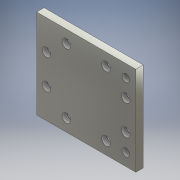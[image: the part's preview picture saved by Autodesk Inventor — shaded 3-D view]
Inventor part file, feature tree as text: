
AUTODESK INVENTOR PART (.ipt)
format: ipt  version: 2017 (Build 210142000, 142)  size: 217,088 bytes
history: native  units: mm
features: extrude x3, sketch x3, projected_geometry x1
ambient origin geometry x8: Origin, YZ Plane, XZ Plane, XY Plane, X Axis, Y Axis, Z Axis, Center Point
bodies: Solid1 (feature_tree)
feature tree (7):
  extrude  "Extrusion1"  Depth=3.0mm TaperAngle=0.0deg
  extrude  "Extrusion2"  Depth=3.0mm TaperAngle=0.0deg
  extrude  "Extrusion4"  Depth=3.0mm
  sketch  "Sketch1"  dims[d0=40.0mm d1=36.0mm d2=3.0mm d3=0.0mm]
  sketch  "Sketch2"  dims[d4=4.0mm d5=12.0mm d6=12.0mm d7=6.0mm d8=6.0mm d9=3.0mm d10=0.0mm]
  sketch  "Sketch5"  dims[d11=6.0mm d12=3.0mm d13=0.0mm d14=0.0mm d15=5.0mm d16=4.0mm d17=4.0mm d18=12.0mm d19=4.0mm d20=24.0mm d21=12.0mm d22=5.0mm d23=12.0mm d24=31.0mm d25=28.0mm d26=5.0mm d27=28.0mm d28=31.0mm d29=36.0mm d30=36.0mm d31=5.0mm d32=36.0mm d33=31.0mm d34=5.0mm d35=0.0mm d36=35.939652mm d37=4.060348mm d38=35.939652mm d39=3.5mm d40=0.0mm d41=0.0mm d42=3.5mm d43=0.0mm d44=0.0mm d45=6.0mm d46=3.5mm d47=0.0mm d48=0.0mm d49=6.0mm d50=3.5mm d51=0.0mm d52=0.0mm d53=6.0mm d54=3.5mm d55=0.0mm d56=0.0mm d57=6.0mm d58=3.5mm d59=0.0mm d60=0.0mm d61=6.0mm d62=3.5mm d63=0.0mm d64=0.0mm d65=6.0mm d66=3.5mm d67=0.0mm d68=0.0mm d69=6.0mm d72=2.0mm d73=0.0mm d74=68.0mm d75=67.0mm d76=68.0mm d77=67.0mm d78=68.0mm d79=67.0mm d80=75.939652mm d81=60.0mm]
  projected_geometry  "Projected Loop1"
